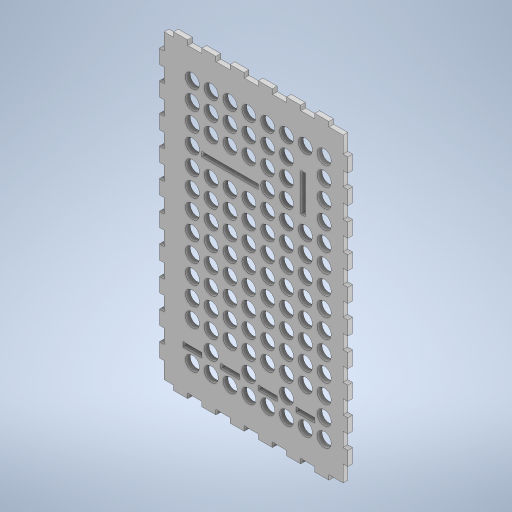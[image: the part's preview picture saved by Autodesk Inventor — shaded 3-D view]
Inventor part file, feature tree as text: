
AUTODESK INVENTOR PART (.ipt)
format: ipt  version: 2023 (Build 270158000, 158)  size: 664,576 bytes
history: native  units: mm
features: reference x24, other x5, extrude x4, sketch x4
ambient origin geometry x8: Origin, YZ Plane, XZ Plane, XY Plane, X Axis, Y Axis, Z Axis, Center Point
bodies: Solid1 (feature_tree)
feature tree (37):
  extrude  "Extrusion1"  Depth=330.0mm
  extrude  "Extrusion2"  TaperAngle=0.0deg  [1 undecoded]
  extrude  "Extrusion6"  Depth=5.0mm
  extrude  "Extrusion7"  Depth=22.5mm
  sketch  "Sketch1"  dims[d0=200.0mm d1=330.0mm]
  sketch  "Sketch2"  dims[d2=5.0mm d3=0.0mm]
  sketch  "Sketch6"  dims[d4=0.0mm d5=5.0mm]
  reference  "Reference1"
  reference  "Reference2"
  reference  "Reference3"
  reference  "Reference4"
  reference  "Reference5"
  reference  "Reference6"
  reference  "Reference7"
  reference  "Reference8"
  reference  "Reference9"
  reference  "Reference10"
  reference  "Reference11"
  reference  "Reference12"
  reference  "Reference13"
  reference  "Reference14"
  reference  "Reference15"
  reference  "Reference16"
  reference  "Reference17"
  reference  "Reference18"
  reference  "Reference19"
  reference  "Reference20"
  reference  "Reference21"
  reference  "Reference22"
  reference  "Reference23"
  reference  "Reference24"
  sketch  "Sketch7"  dims[d6=0.0mm d7=22.5mm d8=5.0mm d9=15.0mm d10=15.0mm d11=90.0mm d13=30.0mm d14=10.0mm d16=10.0mm d18=22.5mm d19=5.0mm d20=20.0mm d21=0.0mm d70=5.0mm d71=15.0mm d72=70.0mm d74=30.0mm d75=10.0mm d77=10.0mm d79=5.0mm d80=15.0mm d81=70.0mm d83=30.0mm d84=10.0mm d86=10.0mm d88=10.0mm d89=0.0mm d90=30.0mm d91=30.0mm d92=15.0mm d93=140.0mm d95=20.0mm d96=80.0mm d98=20.0mm d101=10.0mm d102=0.0mm]
  other  "<userpath>\OneDrive\ClawdDrive\Objet3D\Clawd4\Assembly1.iam"
  other  "Assembly1.iam"
  other  "PSUbackplate:1"
  other  "PSUSideplate:1"
  other  "motherBoardHolder:1"
note: 1 required parameter value undecoded (feature->parameter linkage not recoverable at this tier; creation-order binding heuristic only, values carry confidence <= 0.55)
